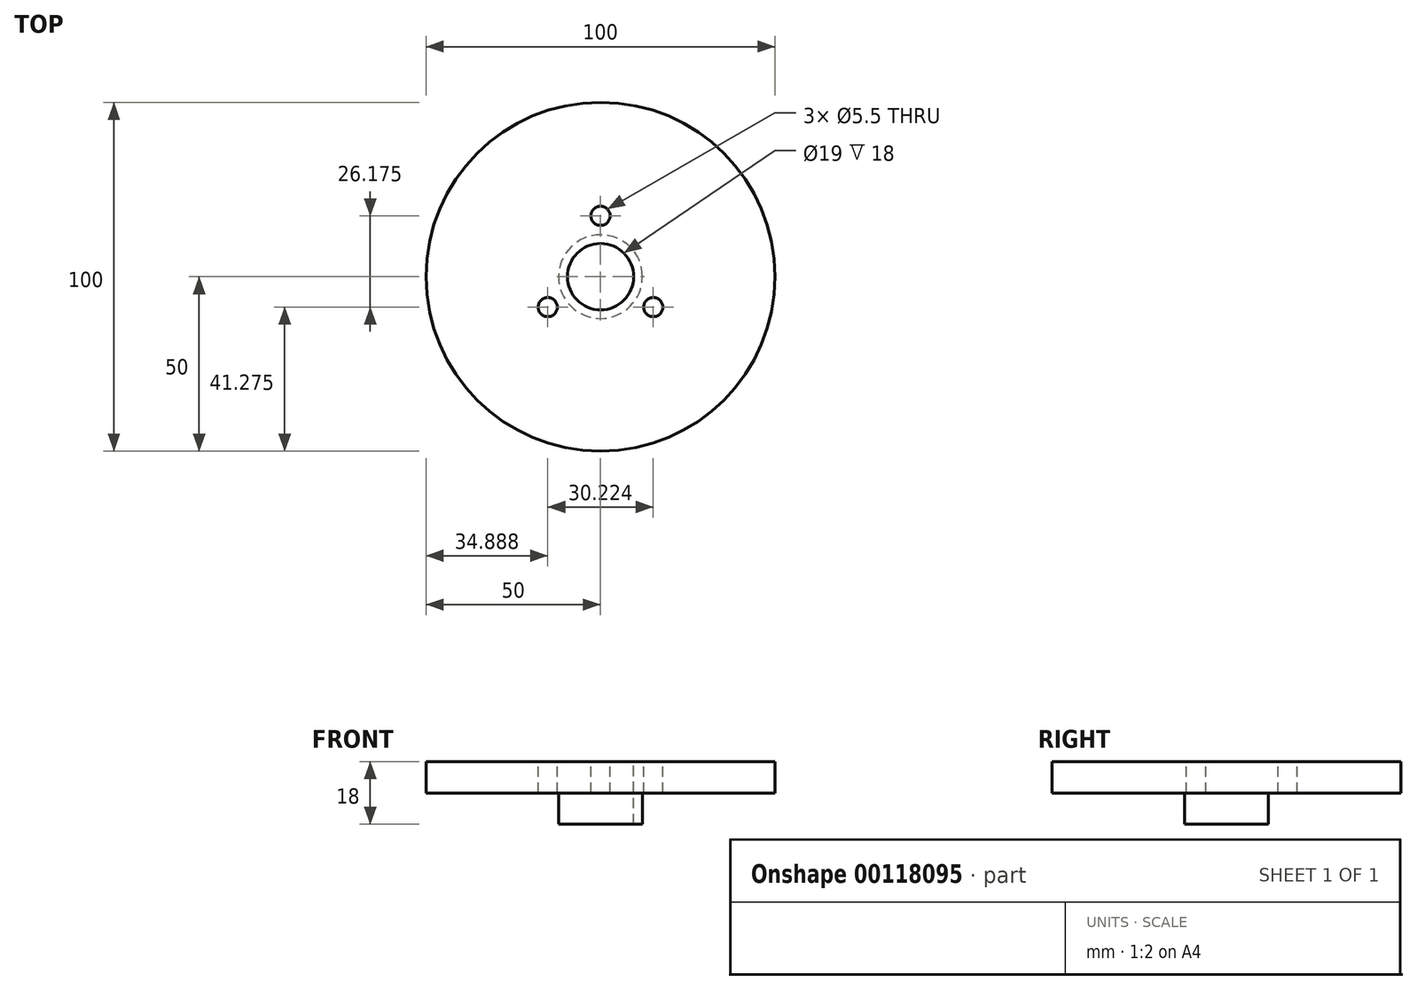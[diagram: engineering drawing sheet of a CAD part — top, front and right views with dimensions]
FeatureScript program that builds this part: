
annotation { "Feature Type Name" : "Feature", "Feature Type Description" : "" }
export const myFeature = defineFeature(function(context is Context, id is Id, definition is map)
    precondition{}
    {
        {
            var Q0;
            Q0=qCreatedBy(makeId("Right.planeOp"),FACE);
            var sketch = newSketch(context, id + "F0", { "sketchPlane" : qUnion([Q0])});
            skLineSegment(sketch, "E0", {"start": v(0, 0) * mm, "end": v(-6, 0) * mm, "construction": true});
            skLineSegment(sketch, "E1", {"start": v(-6, 0) * mm, "end": v(-50, 0) * mm});
            skLineSegment(sketch, "E2", {"start": v(-50, 0) * mm, "end": v(-50, -9) * mm});
            skLineSegment(sketch, "E3", {"start": v(-50, -9) * mm, "end": v(-12, -9) * mm});
            skLineSegment(sketch, "E4", {"start": v(-12, -9) * mm, "end": v(-12, -18) * mm});
            skLineSegment(sketch, "E5", {"start": v(-12, -18) * mm, "end": v(-6, -18) * mm});
            skLineSegment(sketch, "E6", {"start": v(-6, -18) * mm, "end": v(-6, 0) * mm});
            skLineSegment(sketch, "E7", {"start": v(0, 0) * mm, "end": v(0, -18.21) * mm, "construction": true});
            skSolve(sketch);
        }
        {
            var Q0;
            Q0=makeQuery(id+"F0.imprint","IMPRINT",FACE,{"disambiguationData":[TD([[makeQuery(id+"F0.imprint","IMPRINT",EDGE,{"derivedFrom":sQuery(id+"F0.wireOp",EDGE,"E1")}),1.0]])]});
            var Q1;
            Q1=sQuery(id+"F0.wireOp",EDGE,"E7");
            revolve(context, id + "F1", {"entities" : qUnion([Q0]), "axis" : qUnion([Q1]), "revolveType" : RevolveType.FULL});
        }
        {
            var Q0;
            Q0=makeQuery(id+"F1.opRevolve","SWEPT_FACE",FACE,{"disambiguationData":[OSD([sQuery(id+"F0.wireOp",EDGE,"E1")])]});
            var sketch = newSketch(context, id + "F2", { "sketchPlane" : qUnion([Q0])});
            skPoint(sketch, "E8", {"position": v(0, 0) * mm});
            skCircle(sketch, "E9", {"center": v(0, 0) * mm, "radius": 8.52 * mm, "construction": true});
            skSolve(sketch);
        }
        {
            var Q0;
            Q0=sQuery(id+"F2.wireOp",VERTEX,"E8");
            var Q1;
            Q1=makeQuery(id+"F1.opRevolve","SWEPT_BODY",BODY,{"disambiguationData":[OSD([sQuery(id+"F0.wireOp",EDGE,"E1"),sQuery(id+"F0.wireOp",EDGE,"E2"),sQuery(id+"F0.wireOp",EDGE,"E3"),sQuery(id+"F0.wireOp",EDGE,"E4"),sQuery(id+"F0.wireOp",EDGE,"E5"),sQuery(id+"F0.wireOp",EDGE,"E6")])]});
            hole(context, id + "F3", {"style" : HoleStyle.SIMPLE, "endStyle" : HoleEndStyle.THROUGH, "standardTappedOrClearance" : lookupTablePath({ "standard" : "ISO", "size" : "19", "type" : "Drilled" }), "standardBlindInLast" : lookupTablePath({ "standard" : "ISO", "size" : "19", "type" : "Drilled" }), "holeDiameter" : 19 * mm, "startFromSketch" : true, "locations" : qUnion([Q0]), "scope" : qUnion([Q1]), "isTappedThrough" : true});
        }
        {
            var Q0;
            Q0=makeQuery(id+"F1.opRevolve","SWEPT_FACE",FACE,{"disambiguationData":[OSD([sQuery(id+"F0.wireOp",EDGE,"E1")])]});
            var sketch = newSketch(context, id + "F4", { "sketchPlane" : qUnion([Q0])});
            skCircle(sketch, "E10", {"center": v(0, 0) * mm, "radius": 17.45 * mm, "construction": true});
            skLineSegment(sketch, "E11", {"start": v(0, 0) * mm, "end": v(0, 17.45) * mm, "construction": true});
            skLineSegment(sketch, "E12", {"start": v(0, 0) * mm, "end": v(15.11, -8.72) * mm, "construction": true});
            skLineSegment(sketch, "E13", {"start": v(0, 0) * mm, "end": v(-15.11, -8.73) * mm, "construction": true});
            skCircle(sketch, "E14", {"center": v(0, 17.45) * mm, "radius": 2.6 * mm});
            skCircle(sketch, "E15", {"center": v(-15.11, -8.73) * mm, "radius": 2.6 * mm});
            skCircle(sketch, "E16", {"center": v(15.11, -8.72) * mm, "radius": 2.6 * mm});
            skSolve(sketch);
        }
        {
            var Q0;
            Q0=sQuery(id+"F4.wireOp",VERTEX,"E15.center");
            var Q1;
            Q1=sQuery(id+"F4.wireOp",VERTEX,"E11.end");
            var Q2;
            Q2=sQuery(id+"F4.wireOp",VERTEX,"E16.center");
            var Q3;
            Q3=makeQuery(id+"F1.opRevolve","SWEPT_BODY",BODY,{"disambiguationData":[OSD([sQuery(id+"F0.wireOp",EDGE,"E1"),sQuery(id+"F0.wireOp",EDGE,"E2"),sQuery(id+"F0.wireOp",EDGE,"E3"),sQuery(id+"F0.wireOp",EDGE,"E4"),sQuery(id+"F0.wireOp",EDGE,"E5"),sQuery(id+"F0.wireOp",EDGE,"E6")])]});
            hole(context, id + "F5", {"style" : HoleStyle.SIMPLE, "endStyle" : HoleEndStyle.THROUGH, "standardTappedOrClearance" : lookupTablePath({ "standard" : "ISO", "fit" : "Normal", "size" : "M5", "type" : "Clearance" }), "standardBlindInLast" : lookupTablePath({ "fit" : "Standard", "standard" : "ISO", "size" : "M5", "type" : "Clearance" }), "holeDiameter" : 5.5 * mm, "startFromSketch" : true, "locations" : qUnion([Q0, Q1, Q2]), "scope" : qUnion([Q3]), "isTappedThrough" : true});
        }
    });
